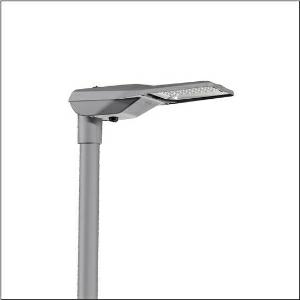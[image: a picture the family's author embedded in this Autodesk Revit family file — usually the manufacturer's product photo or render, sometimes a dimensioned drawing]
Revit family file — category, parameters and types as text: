
# Revit family: streetlight_sl_21_mini___st1_0a_5xe2d33t08jb_5341
name_source: partatom
category: Lighting Fixtures
units: mm (PartAtom-declared; Revit-internal decimal feet)

## family parameters
Cut with Voids When Loaded = No
Host = Face
Light Source = No
Part Type = Normal
Room Calculation Point = No
Round Connector Dimension = Use Diameter
Shared = No

## types (1)
- --- (1 x LED, 12940 lm, 88.6 W, 3000K)
    Apparent Load = 89 VA
    CIE Flux Codes = 40 73 97 100 100
    Color Rendering = 70
    Color Temperature = 3000K
    Default Elevation = 1800 mm
    Description = Streetlight SL 21 mini, mast luminaire, primary light control with lens, of PMMA, primary optical cover: cover, of toughened safety glass, transparent, light distribution: ST1.0a, light emission: direct distribution, primary light characteristic: asymmetric, installation type: side-entry, post-top, LED, High Power LED, rated luminous flux: 12.940lm, luminous efficacy: 146lm/W, light colour: 730, colour temperature: 3000K, control gear: D4i, control: flexible luminous flux parameterisation, time-dependent luminous flux control, constant luminous flux control, overheat protection, pre-setting: logarithmic dimming characteristic, mains connection: 220..240V, AC, 50/60Hz, start of lifetime: 89W, end of service life: 92W, reduction: 41W, luminaire housing, of diecast aluminium, powder-coated, SITECO metallic grey (DB 702S), corrosivity category C5 high according to DIN EN ISO 12944, please order mast flange separately, inclination adjustable: 0°, 5°, 10°, 15°, sealing non-destructively replaceable, multi-level sealing system, length: 628mm, width: 235mm, height: 110mm, mast flange for spigot size: 42mm (side-entry): 5XC10008XM4, 60/48mm (side-entry/post-top): 5XC10108XM2, 76/60mm (side-entry/post-top): 5XC10108XM1, mounting height: 4..8m, Smart Interface below and above, protection rating (complete): IP66, insulation class (complete): insulation class II (safety insulation), certification: CE, ENEC, ENEC+, VDE, impact resistance: IK10, permissible operating ambient temperature for outdoor applications: -40..+50°C, standard-compliant lighting for roads and squares, packaging unit: 1 piece

Light Distribution: ST1.0a
    Height = 110 mm
    Lamp = 1 x LED
    Lamp Light Flux = 12940 lm
    Lamp Power = 88.6 W
    Lamp count = 1
    Length = 625 mm
    Luminous efficacy = 146 lm/W
    Manufacturer = Siteco
    ModVariant = No
    Model = 5XE2D33T08JB
    Number of Poles = 1
    OnlyDefault = Yes
    Power Factor = 1
    Product Name = Streetlight SL 21 mini | ST1.0a
    Product group = mast luminaire | pylon top
    ProductGroupID = 6100
    Protection Class = Protection class II
    Protection Degree = IP 66
    RLX_Detail_Level = 1
    RLX_Emergency_Light_Flux = 0 lm
    RLX_Emergency_Type = 0
    RLX_Emergency_Type_DB = No
    RlxData = <blob elided: 26457 chars, md5=13acd1df>
    Socket = socket
    Standby Power = 0 W
    System Light Flux = 12940 lm
    System Power = 89 W
    Type Comments = factory setting: luminous flux: 100 % | dim-lin: 254 | 915 mA
    Type Image = l_1003514.jpg
    URL = http://relux.com
    VarID = @adj_031235
    Voltage = 0 V
    Weight = 0.00 kg
    Width = 234 mm

## geometry (parser evidence)
native form markers: Blend x4, Sweep x10
no freeform markers — native parametric forms only
